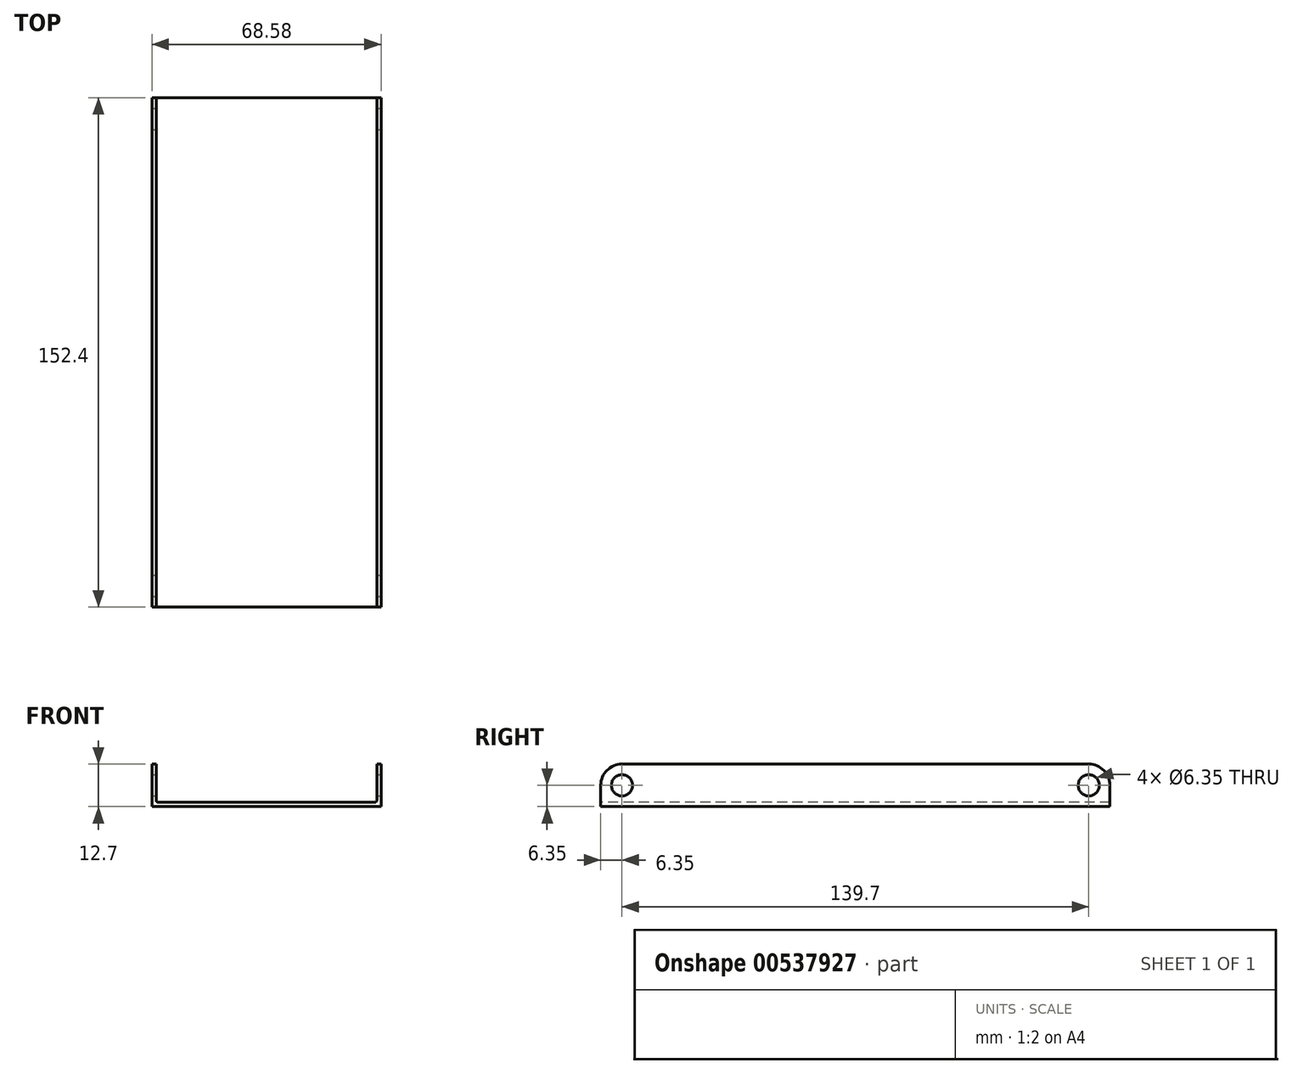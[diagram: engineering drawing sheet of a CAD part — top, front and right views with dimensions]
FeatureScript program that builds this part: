
annotation { "Feature Type Name" : "Feature", "Feature Type Description" : "" }
export const myFeature = defineFeature(function(context is Context, id is Id, definition is map)
    precondition{}
    {
        {
            var Q0;
            Q0=qCreatedBy(makeId("Front.planeOp"),FACE);
            var sketch = newSketch(context, id + "F0", { "sketchPlane" : qUnion([Q0])});
            skLineSegment(sketch, "E0", {"start": v(0, 0) * mm, "end": v(-68.58, 0) * mm});
            skLineSegment(sketch, "E1", {"start": v(-68.58, 0) * mm, "end": v(-68.58, 12.7) * mm});
            skLineSegment(sketch, "E2", {"start": v(-68.58, 12.7) * mm, "end": v(-67.31, 12.7) * mm});
            skLineSegment(sketch, "E3", {"start": v(-67.31, 12.7) * mm, "end": v(-67.31, 1.9) * mm});
            skLineSegment(sketch, "E4", {"start": v(-66.68, 1.27) * mm, "end": v(-1.9, 1.27) * mm});
            skLineSegment(sketch, "E5", {"start": v(-1.27, 1.9) * mm, "end": v(-1.27, 12.7) * mm});
            skLineSegment(sketch, "E6", {"start": v(-1.27, 12.7) * mm, "end": v(0, 12.7) * mm});
            skLineSegment(sketch, "E7", {"start": v(0, 12.7) * mm, "end": v(0, 0) * mm});
            skPoint(sketch, "E8.visualSharp", {"position": v(-1.27, 1.27) * mm});
            skArc(sketch, "E8.filletArc", {"start": v(-1.9, 1.27) * mm, "mid": v(-1.46, 1.46) * mm, "end": v(-1.27, 1.9) * mm});
            skPoint(sketch, "E9.visualSharp", {"position": v(-67.31, 1.27) * mm});
            skArc(sketch, "E9.filletArc", {"start": v(-67.3, 1.9) * mm, "mid": v(-67.12, 1.46) * mm, "end": v(-66.68, 1.27) * mm});
            skSolve(sketch);
        }
        {
            var Q0;
            Q0 = qSketchRegion(id + "F0", true);
            extrude(context, id + "F1", {"entities" : qUnion([Q0]), "oppositeDirection" : true, "depth" : 152.4 * mm, "offsetDistance" : 25.4 * mm});
        }
        {
            var Q0;
            Q0=makeQuery(id+"F1.opExtrude","SWEPT_FACE",FACE,{"disambiguationData":[OSD([sQuery(id+"F0.wireOp",EDGE,"E7")])]});
            var sketch = newSketch(context, id + "F2", { "sketchPlane" : qUnion([Q0])});
            skCircle(sketch, "E10", {"center": v(6.35, 6.35) * mm, "radius": 3.18 * mm});
            skPoint(sketch, "E10.centerSnap0", {"position": v(0, 6.35) * mm});
            skPoint(sketch, "E11.visualSharp", {"position": v(0, 12.7) * mm});
            skArc(sketch, "E11.filletArc", {"start": v(6.35, 12.7) * mm, "mid": v(1.86, 10.84) * mm, "end": v(0, 6.35) * mm});
            skLineSegment(sketch, "E12", {"start": v(0, 6.35) * mm, "end": v(0, 12.7) * mm});
            skLineSegment(sketch, "E13", {"start": v(0, 12.7) * mm, "end": v(6.35, 12.7) * mm});
            skLineSegment(sketch, "E14", {"start": v(76.2, 12.7) * mm, "end": v(76.2, 0) * mm, "construction": true});
            skCircle(sketch, "E15.MirrorC", {"center": v(146.05, 6.35) * mm, "radius": 3.18 * mm});
            skArc(sketch, "E16.MirrorCS", {"start": v(146.05, 12.7) * mm, "mid": v(150.54, 10.84) * mm, "end": v(152.4, 6.35) * mm});
            skLineSegment(sketch, "E17.MirrorCS", {"start": v(152.4, 6.35) * mm, "end": v(152.4, 12.7) * mm});
            skLineSegment(sketch, "E18.MirrorCS", {"start": v(152.4, 12.7) * mm, "end": v(146.05, 12.7) * mm});
            skSolve(sketch);
        }
        {
            var Q0;
            Q0 = qSketchRegion(id + "F2", true);
            extrude(context, id + "F3", {"entities" : qUnion([Q0]), "operationType" : NewBodyOperationType.REMOVE, "endBound" : BoundingType.THROUGH_ALL, "oppositeDirection" : true, "depth" : 25.4 * mm, "offsetDistance" : 25.4 * mm});
        }
    });
